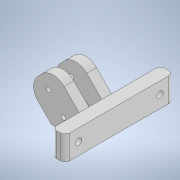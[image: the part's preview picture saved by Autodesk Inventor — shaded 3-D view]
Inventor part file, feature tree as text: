
AUTODESK INVENTOR PART (.ipt)
format: ipt  version: 2022 (Build 260153000, 153)  size: 241,152 bytes
history: native  units: in
note: dims shown in document units (in); Inventor stores cm internally (conversion verified against a paired STEP export)
features: plane x4, sketch x4, projected_geometry x4, hole x2, mirror x2, extrude x1, fillet x1
ambient origin geometry x8: Origin, YZ Plane, XZ Plane, XY Plane, X Axis, Y Axis, Z Axis, Center Point
bodies: Body1 (feature_tree)
feature tree (18):
  plane  "Work Plane1"
  hole  "Hole1"  [1 undecoded]
  extrude  "Extrusion4"  Depth=0.1575in
  plane  "Work Plane2"
  mirror  "Mirror1"
  fillet  "Fillet1"  Radius=0.3543in
  hole  "Hole5"  [1 undecoded]
  plane  "Work Plane3"
  mirror  "Mirror2"
  sketch  "Sketch1"  dims[d0=-0.2559in d1=0.5118in d2=0.0in]
  sketch  "Sketch3"  dims[d5=0.0996in d6=0.2362in d7=0.1575in d8=0.0787in d9=90.0deg d10=0.315in d11=0.8108in]
  sketch  "Sketch5"  dims[d19=0.0996in d20=0.2362in d21=0.1575in d22=0.0787in d23=90.0deg d24=0.315in d25=0.8108in d26=0.3543in d27=0.3543in]
  projected_geometry  "Projected Loop1"
  sketch  "Sketch8"  dims[d28=0.0787in d29=0.0787in d30=0.0394in d31=0.3937in d32=0.0in d35=0.2756in d36=0.2756in d38=0.2067in d39=0.5748in d40=0.3287in d41=0.1417in d42=0.2362in d43=0.2559in d44=0.1181in d45=0.6181in d46=0.3937in d47=0.0in d48=0.1033in d49=0.1033in d50=0.938in d51=0.3346in d52=0.2559in d53=0.5906in]
  projected_geometry  "Projected Loop11"
  projected_geometry  "Projected Loop12"
  projected_geometry  "Projected Loop13"
  plane  "Work Plane4"
note: 2 required parameter values undecoded (feature->parameter linkage not recoverable at this tier; creation-order binding heuristic only, values carry confidence <= 0.55)
